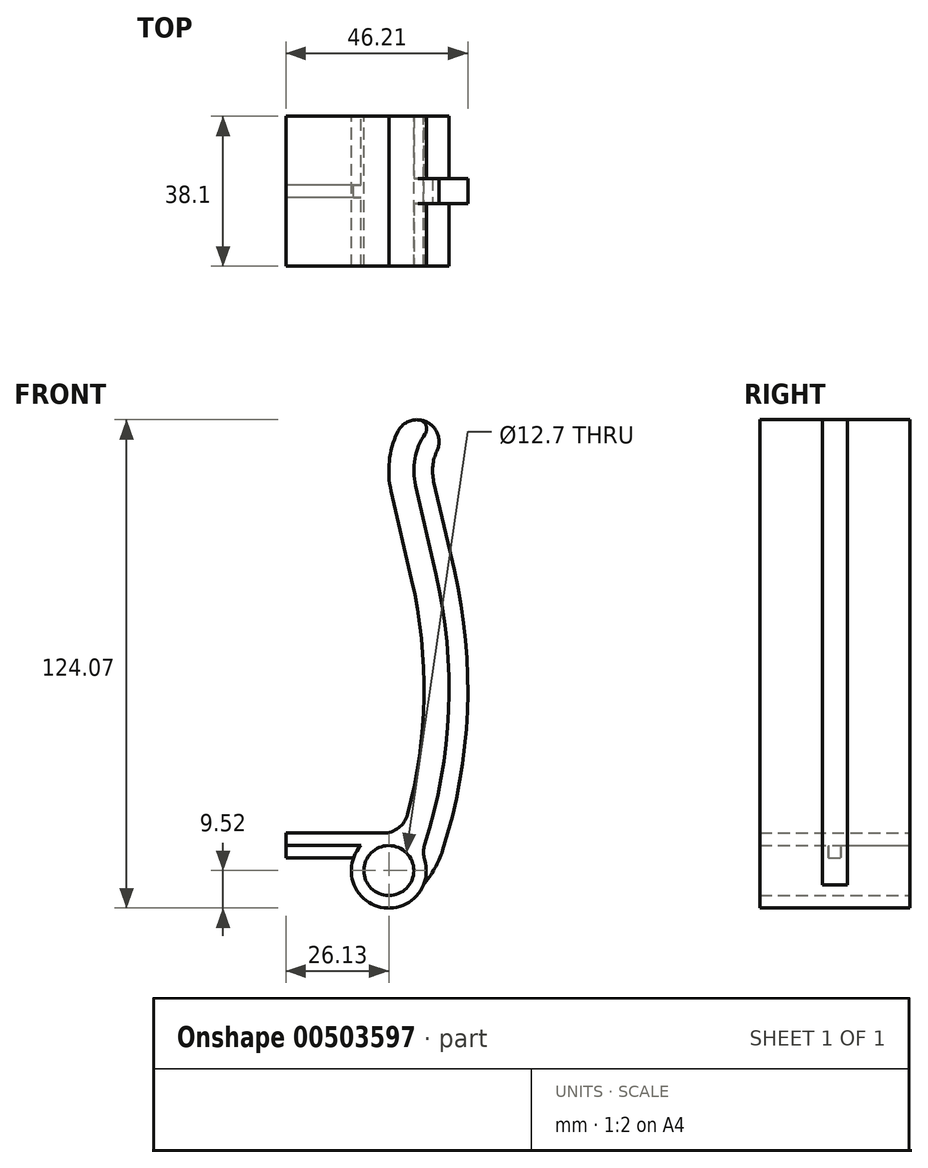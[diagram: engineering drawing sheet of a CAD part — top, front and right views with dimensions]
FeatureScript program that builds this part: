
annotation { "Feature Type Name" : "Feature", "Feature Type Description" : "" }
export const myFeature = defineFeature(function(context is Context, id is Id, definition is map)
    precondition{}
    {
        {
            var Q0;
            Q0=qCreatedBy(makeId("Front.planeOp"),FACE);
            var sketch = newSketch(context, id + "F0", { "sketchPlane" : qUnion([Q0])});
            skCircle(sketch, "E0", {"center": v(19.05, 0) * mm, "radius": 6.35 * mm});
            skArc(sketch, "E1", {"start": v(25.4, 117.47) * mm, "mid": v(19.87, 107.67) * mm, "end": v(19.64, 96.42) * mm});
            skArc(sketch, "E2", {"start": v(19.05, 0) * mm, "mid": v(27.64, 36.46) * mm, "end": v(24.86, 73.81) * mm});
            skLineSegment(sketch, "E3", {"start": v(19.64, 96.42) * mm, "end": v(24.86, 73.81) * mm});
            skLineSegment(sketch, "E4", {"start": v(0, 0) * mm, "end": v(0, 117.48) * mm, "construction": true});
            skLineSegment(sketch, "E5", {"start": v(25.4, 117.48) * mm, "end": v(25.4, 126.45) * mm, "construction": true});
            skLineSegment(sketch, "E6", {"start": v(19.05, 0) * mm, "end": v(33.6, 36) * mm, "construction": true});
            skCircle(sketch, "E7", {"center": v(19.05, 0) * mm, "radius": 9.53 * mm});
            skLineSegment(sketch, "E8", {"start": v(19.05, 9.52) * mm, "end": v(-7.08, 9.52) * mm});
            skLineSegment(sketch, "E9", {"start": v(19.05, 101.6) * mm, "end": v(19.05, 0) * mm, "construction": true});
            skLineSegment(sketch, "E10", {"start": v(42.07, 101.6) * mm, "end": v(0, 101.6) * mm, "construction": true});
            skCircle(sketch, "E11.MirrorC", {"center": v(-19.05, 0) * mm, "radius": 9.53 * mm, "construction": true});
            skCircle(sketch, "E12", {"center": v(19.05, 0) * mm, "radius": 27.81 * mm, "construction": true});
            skSolve(sketch);
        }
        {
            var Q0;
            Q0=makeQuery(id+"F0.imprint","IMPRINT",FACE,{"disambiguationData":[TD([[makeQuery(id+"F0.imprint","IMPRINT",EDGE,{"derivedFrom":sQuery(id+"F0.wireOp",EDGE,"E0")}),-1.0]])]});
            extrude(context, id + "F1", {"entities" : qUnion([Q0]), "depth" : 38.1 * mm, "offsetDistance" : 25.4 * mm, "symmetric" : true});
        }
        {
            var Q0;
            Q0=sQuery(id+"F0.wireOp",VERTEX,"E5.start");
            var Q1;
            Q1=sQuery(id+"F0.wireOp",EDGE,"E1");
            cPlane(context, id + "F2", {"entities" : qUnion([Q0, Q1]), "cplaneType" : CPlaneType.CURVE_POINT, "offset" : 25.4 * mm, "width" : 152.4 * mm, "height" : 152.4 * mm});
        }
        {
            var Q0;
            Q0=qCreatedBy(id+"F2.planeOp",FACE);
            var sketch = newSketch(context, id + "F3", { "sketchPlane" : qUnion([Q0])});
            skLineSegment(sketch, "E13.bottom", {"start": v(-62.62, 19.05) * mm, "end": v(-56.27, 19.05) * mm});
            skLineSegment(sketch, "E13.top", {"start": v(-62.62, -19.05) * mm, "end": v(-56.27, -19.05) * mm});
            skLineSegment(sketch, "E13.left", {"start": v(-62.62, 19.05) * mm, "end": v(-62.62, -19.05) * mm});
            skLineSegment(sketch, "E13.right", {"start": v(-56.27, 19.05) * mm, "end": v(-56.27, -19.05) * mm});
            skLineSegment(sketch, "E14.bottom", {"start": v(-56.27, 3.18) * mm, "end": v(-51.51, 3.18) * mm});
            skLineSegment(sketch, "E14.top", {"start": v(-56.27, -3.18) * mm, "end": v(-51.51, -3.18) * mm});
            skLineSegment(sketch, "E14.left", {"start": v(-56.27, 3.18) * mm, "end": v(-56.27, -3.18) * mm});
            skLineSegment(sketch, "E14.right", {"start": v(-51.51, 3.18) * mm, "end": v(-51.51, -3.18) * mm});
            skPoint(sketch, "E15", {"position": v(-56.27, 0) * mm});
            skSolve(sketch);
        }
        {
            var Q0;
            {var subQ1=sQuery(id+"F3.wireOp",EDGE,"E13.bottom");Q0=makeQuery(id+"F3.imprint","IMPRINT",FACE,{"disambiguationData":[TD([[makeQuery(id+"F3.imprint","IMPRINT",EDGE,{"derivedFrom":subQ1}),-1.0]])]});}
            var Q1;
            Q1=makeQuery(id+"F3.imprint","IMPRINT",FACE,{"disambiguationData":[TD([[makeQuery(id+"F3.imprint","IMPRINT",EDGE,{"derivedFrom":sQuery(id+"F3.wireOp",EDGE,"E14.bottom")}),-1.0]])]});
            var Q2;
            Q2=sQuery(id+"F0.wireOp",EDGE,"E1");
            var Q3;
            Q3=sQuery(id+"F0.wireOp",EDGE,"E3");
            var Q4;
            Q4=sQuery(id+"F0.wireOp",EDGE,"E2");
            sweep(context, id + "F4", {"operationType" : NewBodyOperationType.ADD, "profiles" : qUnion([Q0, Q1]), "path" : qUnion([Q2, Q3, Q4])});
        }
        {
            var Q0;
            Q0=makeQuery(id+"F4.boolean.opBoolean","MERGE",FACE,{"derivedFrom":[makeQuery(id+"F1.opExtrude","CAP_FACE",FACE,{"disambiguationData":[OSD([sQuery(id+"F0.wireOp",EDGE,"E0"),sQuery(id+"F0.wireOp",EDGE,"E7")])],"isStart":false}),makeQuery(id+"F4.opSweep","SWEPT_FACE",FACE,{"disambiguationData":[OSD([sQuery(id+"F0.wireOp",EDGE,"E1"),sQuery(id+"F3.wireOp",EDGE,"E13.bottom")])]})]});
            var sketch = newSketch(context, id + "F5", { "sketchPlane" : qUnion([Q0])});
            skArc(sketch, "E16", {"start": v(31.28, 106.64) * mm, "mid": v(28.6, 114.03) * mm, "end": v(21.22, 111.35) * mm});
            skArc(sketch, "E17.0", {"start": v(37.62, 112.64) * mm, "mid": v(33.88, 110.24) * mm, "end": v(31.28, 106.64) * mm});
            skArc(sketch, "E18.0", {"start": v(29.19, 120.68) * mm, "mid": v(24.57, 116.55) * mm, "end": v(21.22, 111.35) * mm});
            skPoint(sketch, "E19.orphan", {"position": v(19.64, 96.42) * mm});
            skPoint(sketch, "E20.orphan", {"position": v(30.47, 98.92) * mm});
            skLineSegment(sketch, "E21", {"start": v(29.19, 120.68) * mm, "end": v(37.62, 112.64) * mm});
            skPoint(sketch, "E22.orphan", {"position": v(25.4, 117.47) * mm});
            skPoint(sketch, "E23.orphan", {"position": v(33.45, 109.81) * mm});
            skSolve(sketch);
        }
        {
            var Q0;
            Q0 = qSketchRegion(id + "F5", true);
            var Q1;
            Q1=makeQuery(id+"F4.boolean.opBoolean","MERGE",FACE,{"derivedFrom":[makeQuery(id+"F1.opExtrude","CAP_FACE",FACE,{"disambiguationData":[OSD([sQuery(id+"F0.wireOp",EDGE,"E0"),sQuery(id+"F0.wireOp",EDGE,"E7")])],"isStart":true}),makeQuery(id+"F4.opSweep","SWEPT_FACE",FACE,{"disambiguationData":[OSD([sQuery(id+"F0.wireOp",EDGE,"E1"),sQuery(id+"F3.wireOp",EDGE,"E13.top")])]})]});
            extrude(context, id + "F6", {"entities" : qUnion([Q0]), "operationType" : NewBodyOperationType.REMOVE, "endBound" : BoundingType.UP_TO_SURFACE, "oppositeDirection" : true, "depth" : 25.4 * mm, "endBoundEntityFace" : qUnion([Q1]), "offsetDistance" : 25.4 * mm});
        }
        {
            var Q0;
            Q0=sQuery(id+"F0.wireOp",VERTEX,"E8.end");
            var Q1;
            Q1=sQuery(id+"F0.wireOp",EDGE,"E8");
            cPlane(context, id + "F7", {"entities" : qUnion([Q0, Q1]), "cplaneType" : CPlaneType.CURVE_POINT, "offset" : 25.4 * mm, "width" : 152.4 * mm, "height" : 152.4 * mm});
        }
        {
            var Q0;
            Q0=qCreatedBy(id+"F7.planeOp",FACE);
            var sketch = newSketch(context, id + "F8", { "sketchPlane" : qUnion([Q0])});
            skLineSegment(sketch, "E24.bottom", {"start": v(-19.05, 9.52) * mm, "end": v(19.05, 9.52) * mm});
            skLineSegment(sketch, "E24.top", {"start": v(-19.05, 6.35) * mm, "end": v(19.05, 6.35) * mm});
            skLineSegment(sketch, "E24.left", {"start": v(-19.05, 9.52) * mm, "end": v(-19.05, 6.35) * mm});
            skLineSegment(sketch, "E24.right", {"start": v(19.05, 9.52) * mm, "end": v(19.05, 6.35) * mm});
            skLineSegment(sketch, "E25.bottom", {"start": v(-1.59, 6.35) * mm, "end": v(1.59, 6.35) * mm});
            skLineSegment(sketch, "E25.top", {"start": v(-1.59, 3.17) * mm, "end": v(1.59, 3.17) * mm});
            skLineSegment(sketch, "E25.left", {"start": v(-1.59, 6.35) * mm, "end": v(-1.59, 3.17) * mm});
            skLineSegment(sketch, "E25.right", {"start": v(1.59, 6.35) * mm, "end": v(1.59, 3.17) * mm});
            skPoint(sketch, "E26", {"position": v(0, 6.35) * mm});
            skSolve(sketch);
        }
        {
            var Q0;
            Q0 = qSketchRegion(id + "F8", true);
            var Q1;
            Q1=makeQuery(id+"F1.opExtrude","SWEPT_BODY",BODY,{"disambiguationData":[OSD([sQuery(id+"F0.wireOp",EDGE,"E0"),sQuery(id+"F0.wireOp",EDGE,"E7")])]});
            extrude(context, id + "F9", {"entities" : qUnion([Q0]), "operationType" : NewBodyOperationType.ADD, "endBound" : BoundingType.UP_TO_BODY, "oppositeDirection" : true, "depth" : 25.4 * mm, "endBoundEntityBody" : qUnion([Q1]), "offsetDistance" : 25.4 * mm});
        }
        {
            var Q0;
            {var subQ0=sQuery(id+"F0.wireOp",EDGE,"E7");var subQ1=sQuery(id+"F0.wireOp",EDGE,"E0");Q0=makeQuery(id+"Fmr3H8O5dIdzgEA_2.boolean.opBoolean","MERGE",FACE,{"derivedFrom":[makeQuery(id+"F1.opExtrude","CAP_FACE",FACE,{"disambiguationData":[OSD([subQ1,subQ0])],"isStart":false}),makeQuery(id+"Fmr3H8O5dIdzgEA_2.opThicken","SWEPT_FACE",FACE,{"disambiguationData":[OSD([subQ1,subQ0]),TDD([makeQuery(id+"FCQPEc84BeEGUJM_1.opExtrude","CAP_EDGE",EDGE,{"disambiguationData":[OSD([subQ1,subQ0]),OD(0.0)],"isStart":true})])]})]});}
            var sketch = newSketch(context, id + "F10", { "sketchPlane" : qUnion([Q0])});
            skCircle(sketch, "E27.0", {"center": v(19.05, 0) * mm, "radius": 6.35 * mm});
            skSolve(sketch);
        }
        {
            var Q0;
            Q0 = qSketchRegion(id + "F10", true);
            var Q1;
            {var subQ0=sQuery(id+"F0.wireOp",EDGE,"E7");var subQ1=sQuery(id+"F0.wireOp",EDGE,"E0");Q1=makeQuery(id+"Fmr3H8O5dIdzgEA_2.boolean.opBoolean","MERGE",FACE,{"derivedFrom":[makeQuery(id+"F1.opExtrude","CAP_FACE",FACE,{"disambiguationData":[OSD([subQ1,subQ0])],"isStart":true}),makeQuery(id+"Fmr3H8O5dIdzgEA_2.opThicken","SWEPT_FACE",FACE,{"disambiguationData":[OSD([subQ1,subQ0]),TDD([makeQuery(id+"FCQPEc84BeEGUJM_1.opExtrude","CAP_EDGE",EDGE,{"disambiguationData":[OSD([subQ1,subQ0]),OD(2.0)],"isStart":false})]),ownerDisambiguation([makeQuery(id+"FCQPEc84BeEGUJM_1.opExtrude","SWEPT_FACE",FACE,{"disambiguationData":[OSD([sQuery(id+"F0.wireOp",EDGE,"E1")])]})])]})]});}
            extrude(context, id + "F11", {"entities" : qUnion([Q0]), "operationType" : NewBodyOperationType.REMOVE, "endBound" : BoundingType.UP_TO_SURFACE, "oppositeDirection" : true, "depth" : 13.23 * mm, "endBoundEntityFace" : qUnion([Q1]), "offsetDistance" : 25.4 * mm});
        }
        {
            var Q0;
            {var subQ0=sQuery(id+"F3.wireOp",EDGE,"E13.right");var subQ1=sQuery(id+"F0.wireOp",EDGE,"E1");Q0=makeQuery(id+"F6.boolean.opBoolean","INTERSECT",EDGE,{"derivedFrom":[makeQuery(id+"F4.opSweep","SWEPT_FACE",FACE,{"disambiguationData":[OSD([subQ1,subQ0]),TDD([subQ1,makeQuery(id+"F3.imprint","IMPRINT",EDGE,{"disambiguationData":[TD([[makeQuery(id+"F3.imprint","INTERSECT",VERTEX,{"derivedFrom":[sQuery(id+"F3.wireOp",EDGE,"E13.bottom"),subQ0]}),-1.0]])],"derivedFrom":subQ0})])]}),makeQuery(id+"F6.opExtrude","SWEPT_FACE",FACE,{"disambiguationData":[OSD([sQuery(id+"F5.wireOp",EDGE,"E16")])]})]});}
            var Q1;
            {var subQ0=sQuery(id+"F3.wireOp",EDGE,"E13.right");var subQ1=sQuery(id+"F0.wireOp",EDGE,"E1");Q1=makeQuery(id+"F6.boolean.opBoolean","INTERSECT",EDGE,{"derivedFrom":[makeQuery(id+"F4.opSweep","SWEPT_FACE",FACE,{"disambiguationData":[OSD([subQ1,subQ0]),TDD([subQ1,makeQuery(id+"F3.imprint","IMPRINT",EDGE,{"disambiguationData":[TD([[makeQuery(id+"F3.imprint","INTERSECT",VERTEX,{"derivedFrom":[sQuery(id+"F3.wireOp",EDGE,"E13.top"),subQ0]}),1.0]])],"derivedFrom":subQ0})])]}),makeQuery(id+"F6.opExtrude","SWEPT_FACE",FACE,{"disambiguationData":[OSD([sQuery(id+"F5.wireOp",EDGE,"E16")])]})]});}
            fillet(context, id + "F12", {"entities" : qUnion([Q0, Q1]), "radius" : 2.3 * mm, "tangentPropagation" : true, "allowEdgeOverflow" : false});
        }
        {
            var Q0;
            Q0=makeQuery(id+"F4.boolean.opBoolean","INTERSECT",EDGE,{"derivedFrom":[makeQuery(id+"F1.opExtrude","SWEPT_FACE",FACE,{"disambiguationData":[OSD([sQuery(id+"F0.wireOp",EDGE,"E7")])]}),makeQuery(id+"F4.opSweep","SWEPT_FACE",FACE,{"disambiguationData":[OSD([sQuery(id+"F0.wireOp",EDGE,"E2"),sQuery(id+"F3.wireOp",EDGE,"E13.left")])]})]});
            fillet(context, id + "F13", {"entities" : qUnion([Q0]), "radius" : 6.35 * mm, "tangentPropagation" : true, "allowEdgeOverflow" : false});
        }
        {
            var Q0;
            Q0=makeQuery(id+"F4.opSweep","CAP_EDGE",EDGE,{"disambiguationData":[OSD([sQuery(id+"F0.wireOp",VERTEX,"E2.start"),sQuery(id+"F3.wireOp",EDGE,"E14.right")])],"isStart":false});
            fillet(context, id + "F14", {"entities" : qUnion([Q0]), "radius" : 25.4 * mm, "tangentPropagation" : true, "allowEdgeOverflow" : false});
        }
        {
            var Q0;
            {var subQ0=sQuery(id+"F3.wireOp",EDGE,"E13.right");var subQ1=sQuery(id+"F0.wireOp",EDGE,"E2");Q0=makeQuery(id+"F4.boolean.opBoolean","INTERSECT",EDGE,{"derivedFrom":[makeQuery(id+"F1.opExtrude","SWEPT_FACE",FACE,{"disambiguationData":[OSD([sQuery(id+"F0.wireOp",EDGE,"E7")])]}),makeQuery(id+"F4.opSweep","SWEPT_FACE",FACE,{"disambiguationData":[OSD([subQ1,subQ0]),TDD([subQ1,makeQuery(id+"F3.imprint","IMPRINT",EDGE,{"disambiguationData":[TD([[makeQuery(id+"F3.imprint","INTERSECT",VERTEX,{"derivedFrom":[sQuery(id+"F3.wireOp",EDGE,"E13.bottom"),subQ0]}),-1.0]])],"derivedFrom":subQ0})])]})]});}
            var Q1;
            {var subQ0=sQuery(id+"F3.wireOp",EDGE,"E13.right");var subQ1=sQuery(id+"F0.wireOp",EDGE,"E2");Q1=makeQuery(id+"F4.boolean.opBoolean","INTERSECT",EDGE,{"derivedFrom":[makeQuery(id+"F1.opExtrude","SWEPT_FACE",FACE,{"disambiguationData":[OSD([sQuery(id+"F0.wireOp",EDGE,"E7")])]}),makeQuery(id+"F4.opSweep","SWEPT_FACE",FACE,{"disambiguationData":[OSD([subQ1,subQ0]),TDD([subQ1,makeQuery(id+"F3.imprint","IMPRINT",EDGE,{"disambiguationData":[TD([[makeQuery(id+"F3.imprint","INTERSECT",VERTEX,{"derivedFrom":[sQuery(id+"F3.wireOp",EDGE,"E13.top"),subQ0]}),1.0]])],"derivedFrom":subQ0})])]})]});}
            fillet(context, id + "F15", {"entities" : qUnion([Q0, Q1]), "radius" : 6.35 * mm, "tangentPropagation" : true, "allowEdgeOverflow" : false});
        }
    });
